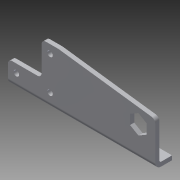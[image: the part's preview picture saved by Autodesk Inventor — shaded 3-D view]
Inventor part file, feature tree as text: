
AUTODESK INVENTOR PART (.ipt)
format: ipt  version: 2014 (Build 180170000, 170)  size: 170,496 bytes
history: native  units: in
note: dims shown in document units (in); Inventor stores cm internally (conversion verified against a paired STEP export)
features: sheet_metal_op x4, other x3, sketch x2, fillet x1
ambient origin geometry x8: Origin, YZ Plane, XZ Plane, XY Plane, X Axis, Y Axis, Z Axis, Center Point
bodies: Solid1 (feature_tree)
feature tree (10):
  sheet_metal_op  "Face1"
  sheet_metal_op  "Flange1"
  fillet  "Fillet2"  Radius=0.5in
  sketch  "Sketch1"  dims[d1=1.0in]
  other  "Plate1"
  sketch  "Sketch2"  dims[d2=1.0in d3=0.5in d4=4.375in d5=0.5in d6=0.75in d7=0.5in d8=90.0deg d9=1.125in d10=0.163in d11=0.25in d12=0.25in d13=0.7874in d15=1.0in d16=0.3937in d18=1.0in d20=0.7874in d22=1.0in d23=0.3937in d25=1.0in d27=0.125in d29=0.125in d30=0.0625in d31=0.25in d32=0.125in d33=0.5in d34=90.0deg d35=0.05in d36=0.5in d37=0.125in d38=0.125in d39=0.125in]
  other  "Plate2"
  sheet_metal_op  "Bend1"
  sheet_metal_op  "Corner1"
  other  "Definition1"
